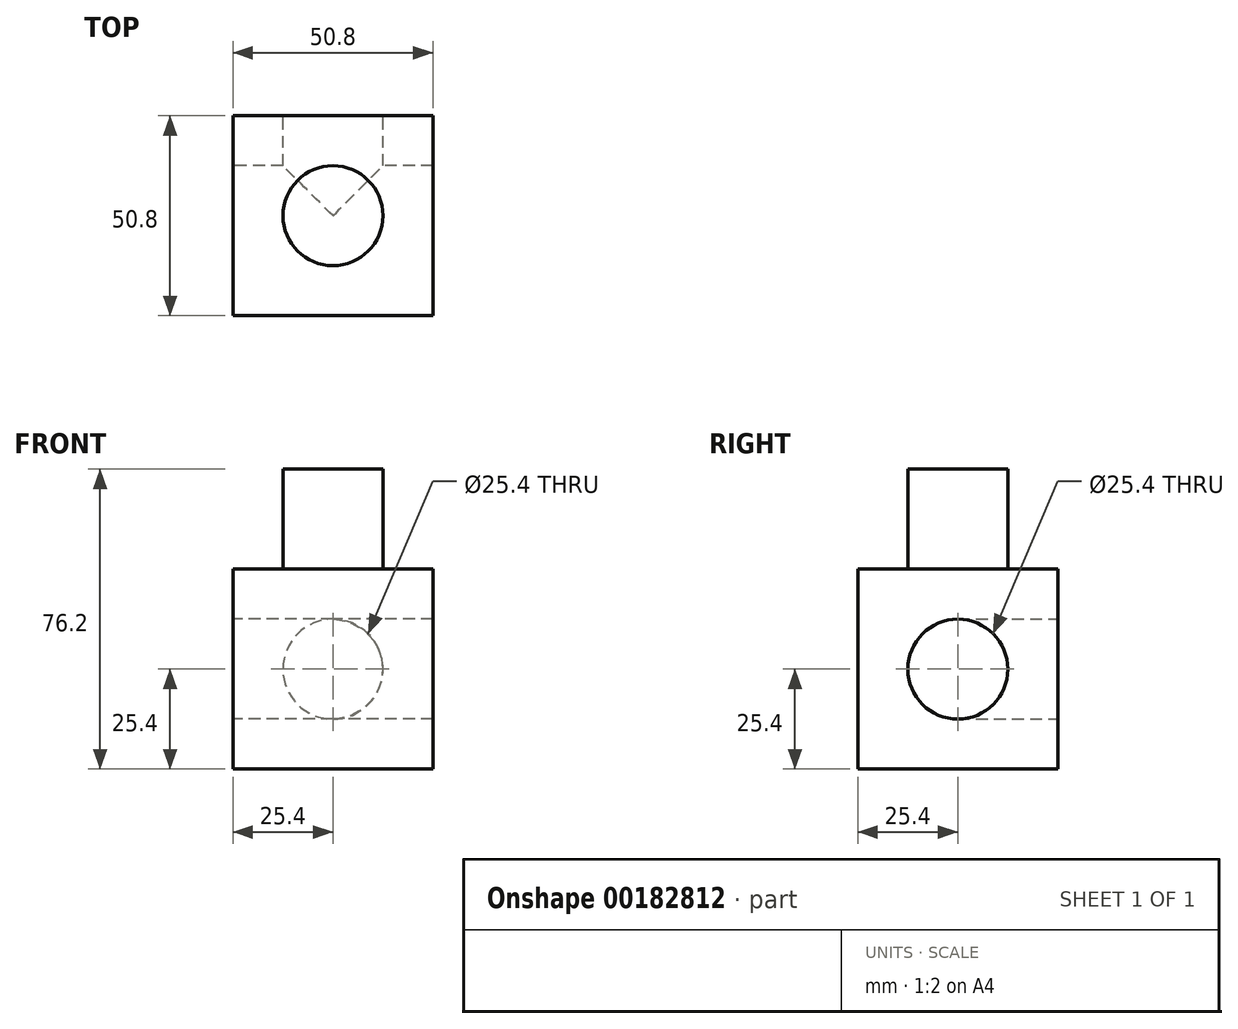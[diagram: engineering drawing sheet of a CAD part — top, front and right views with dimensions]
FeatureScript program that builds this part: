
annotation { "Feature Type Name" : "Feature", "Feature Type Description" : "" }
export const myFeature = defineFeature(function(context is Context, id is Id, definition is map)
    precondition{}
    {
        {
            var Q0;
            Q0=qCreatedBy(makeId("Top.planeOp"),FACE);
            var sketch = newSketch(context, id + "F0", { "sketchPlane" : qUnion([Q0])});
            skLineSegment(sketch, "E0.bottom", {"start": v(0, 0) * mm, "end": v(50.8, 0) * mm});
            skLineSegment(sketch, "E0.top", {"start": v(0, 50.8) * mm, "end": v(50.8, 50.8) * mm});
            skLineSegment(sketch, "E0.left", {"start": v(0, 0) * mm, "end": v(0, 50.8) * mm});
            skLineSegment(sketch, "E0.right", {"start": v(50.8, 0) * mm, "end": v(50.8, 50.8) * mm});
            skSolve(sketch);
        }
        {
            var Q0;
            Q0 = qSketchRegion(id + "F0", true);
            extrude(context, id + "F1", {"entities" : qUnion([Q0]), "depth" : 50.8 * mm});
        }
        {
            var Q0;
            Q0=makeQuery(id+"F1.opExtrude","CAP_FACE",FACE,{"disambiguationData":[OSD([sQuery(id+"F0.wireOp",EDGE,"E0.bottom"),sQuery(id+"F0.wireOp",EDGE,"E0.top"),sQuery(id+"F0.wireOp",EDGE,"E0.left"),sQuery(id+"F0.wireOp",EDGE,"E0.right")])],"isStart":false});
            var sketch = newSketch(context, id + "F2", { "sketchPlane" : qUnion([Q0])});
            skCircle(sketch, "E1", {"center": v(25.4, 25.4) * mm, "radius": 12.7 * mm});
            skSolve(sketch);
        }
        {
            var Q0;
            Q0=makeQuery(id+"F2.imprint","IMPRINT",FACE,{"disambiguationData":[TD([[makeQuery(id+"F2.imprint","IMPRINT",EDGE,{"derivedFrom":sQuery(id+"F2.wireOp",EDGE,"E1")}),1.0]])]});
            extrude(context, id + "F3", {"entities" : qUnion([Q0]), "operationType" : NewBodyOperationType.ADD, "depth" : 25.4 * mm});
        }
        {
            var Q0;
            Q0=makeQuery(id+"F1.opExtrude","SWEPT_FACE",FACE,{"disambiguationData":[OSD([sQuery(id+"F0.wireOp",EDGE,"E0.top")])]});
            var sketch = newSketch(context, id + "F4", { "sketchPlane" : qUnion([Q0])});
            skCircle(sketch, "E2", {"center": v(-25.4, 25.4) * mm, "radius": 12.7 * mm});
            skSolve(sketch);
        }
        {
            var Q0;
            Q0=makeQuery(id+"F4.imprint","IMPRINT",FACE,{"disambiguationData":[TD([[makeQuery(id+"F4.imprint","IMPRINT",EDGE,{"derivedFrom":sQuery(id+"F4.wireOp",EDGE,"E2")}),1.0]])]});
            extrude(context, id + "F5", {"entities" : qUnion([Q0]), "operationType" : NewBodyOperationType.REMOVE, "oppositeDirection" : true, "depth" : 25.4 * mm});
        }
        {
            var Q0;
            Q0=makeQuery(id+"F1.opExtrude","SWEPT_FACE",FACE,{"disambiguationData":[OSD([sQuery(id+"F0.wireOp",EDGE,"E0.left")])]});
            var sketch = newSketch(context, id + "F6", { "sketchPlane" : qUnion([Q0])});
            skCircle(sketch, "E3", {"center": v(-25.4, 25.4) * mm, "radius": 12.7 * mm});
            skSolve(sketch);
        }
        {
            var Q0;
            Q0=makeQuery(id+"F6.imprint","IMPRINT",FACE,{"disambiguationData":[TD([[makeQuery(id+"F6.imprint","IMPRINT",EDGE,{"derivedFrom":sQuery(id+"F6.wireOp",EDGE,"E3")}),1.0]])]});
            extrude(context, id + "F7", {"entities" : qUnion([Q0]), "operationType" : NewBodyOperationType.REMOVE, "oppositeDirection" : true, "depth" : 25.4 * mm});
        }
        {
            var Q0;
            Q0=makeQuery(id+"F1.opExtrude","SWEPT_FACE",FACE,{"disambiguationData":[OSD([sQuery(id+"F0.wireOp",EDGE,"E0.right")])]});
            var sketch = newSketch(context, id + "F8", { "sketchPlane" : qUnion([Q0])});
            skCircle(sketch, "E4", {"center": v(25.4, 25.4) * mm, "radius": 12.7 * mm});
            skSolve(sketch);
        }
        {
            var Q0;
            Q0=makeQuery(id+"F8.imprint","IMPRINT",FACE,{"disambiguationData":[TD([[makeQuery(id+"F8.imprint","IMPRINT",EDGE,{"derivedFrom":sQuery(id+"F8.wireOp",EDGE,"E4")}),1.0]])]});
            extrude(context, id + "F9", {"entities" : qUnion([Q0]), "operationType" : NewBodyOperationType.REMOVE, "oppositeDirection" : true, "depth" : 25.4 * mm});
        }
    });
